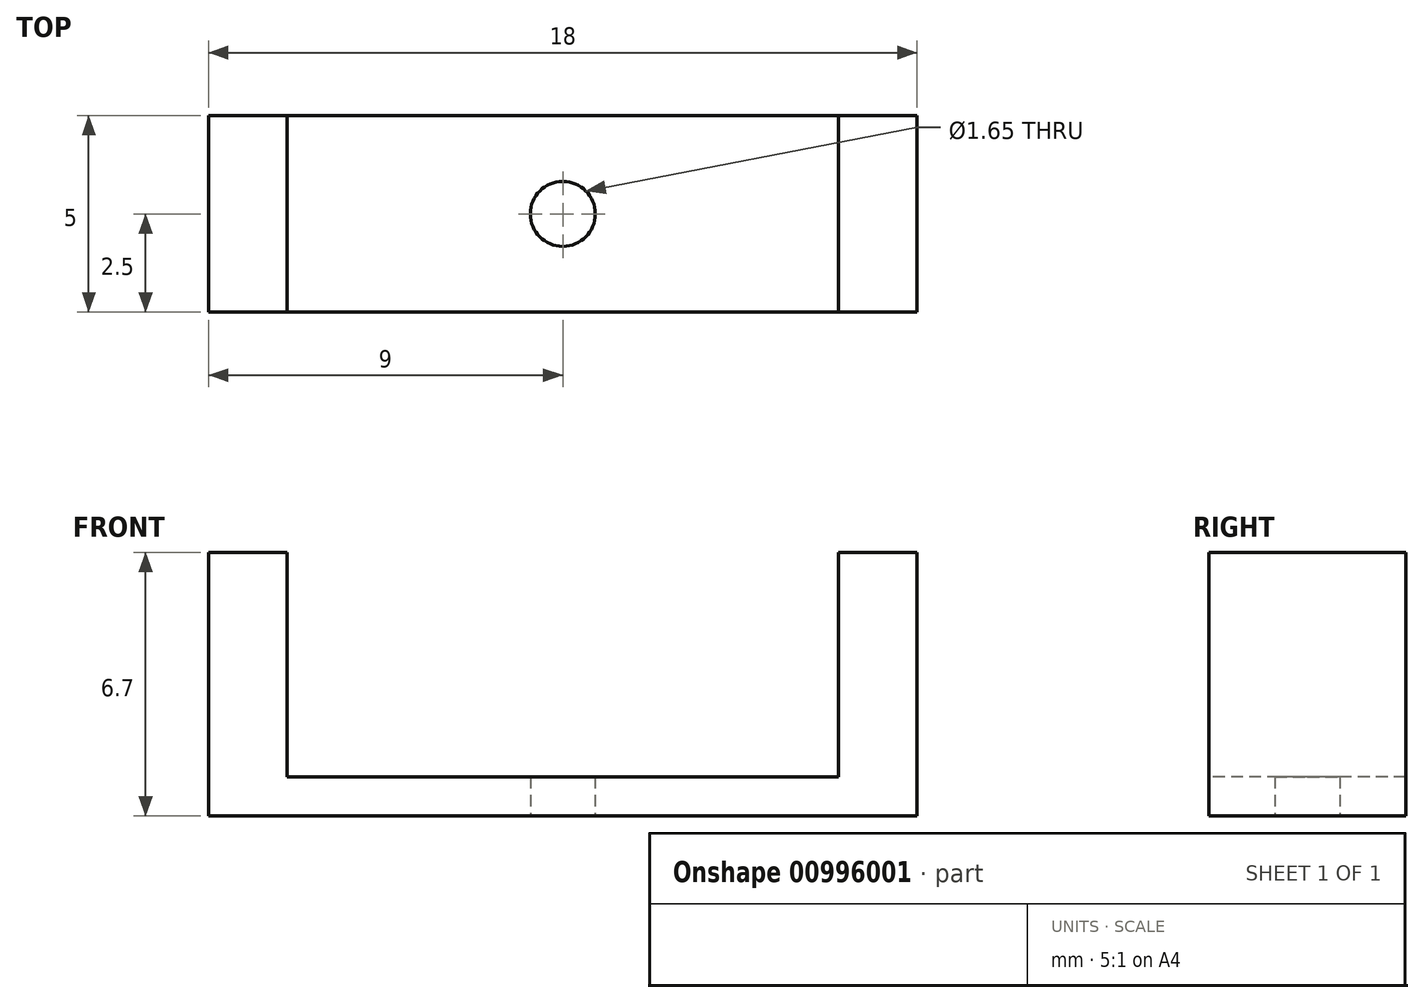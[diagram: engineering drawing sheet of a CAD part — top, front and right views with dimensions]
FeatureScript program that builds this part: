
annotation { "Feature Type Name" : "Feature", "Feature Type Description" : "" }
export const myFeature = defineFeature(function(context is Context, id is Id, definition is map)
    precondition{}
    {
        {
            var Q0;
            Q0=qCreatedBy(makeId("Top.planeOp"),FACE);
            var sketch = newSketch(context, id + "F0", { "sketchPlane" : qUnion([Q0])});
            skLineSegment(sketch, "E0.bottom", {"start": v(9, -2.5) * mm, "end": v(-9, -2.5) * mm});
            skLineSegment(sketch, "E0.top", {"start": v(9, 2.5) * mm, "end": v(-9, 2.5) * mm});
            skLineSegment(sketch, "E0.left", {"start": v(9, -2.5) * mm, "end": v(9, 2.5) * mm});
            skLineSegment(sketch, "E0.right", {"start": v(-9, -2.5) * mm, "end": v(-9, 2.5) * mm});
            skPoint(sketch, "E0.middle", {"position": v(0, 0) * mm});
            skCircle(sketch, "E1", {"center": v(0, 0) * mm, "radius": 0.82 * mm});
            skSolve(sketch);
        }
        {
            var Q0;
            Q0=makeQuery(id+"F0.imprint","IMPRINT",FACE,{"disambiguationData":[TD([[makeQuery(id+"F0.imprint","IMPRINT",EDGE,{"derivedFrom":sQuery(id+"F0.wireOp",EDGE,"E0.bottom")}),-1.0]])]});
            extrude(context, id + "F1", {"entities" : qUnion([Q0]), "depth" : 1 * mm, "offsetDistance" : 25 * mm});
        }
        {
            var Q0;
            Q0=makeQuery(id+"F1.opExtrude","CAP_FACE",FACE,{"disambiguationData":[OSD([sQuery(id+"F0.wireOp",EDGE,"E0.bottom"),sQuery(id+"F0.wireOp",EDGE,"E0.top"),sQuery(id+"F0.wireOp",EDGE,"E0.left"),sQuery(id+"F0.wireOp",EDGE,"E0.right"),sQuery(id+"F0.wireOp",EDGE,"E1")])],"isStart":false});
            var sketch = newSketch(context, id + "F2", { "sketchPlane" : qUnion([Q0])});
            skLineSegment(sketch, "E2.bottom", {"start": v(-9, 2.5) * mm, "end": v(-7, 2.5) * mm});
            skLineSegment(sketch, "E2.top", {"start": v(-9, -2.5) * mm, "end": v(-7, -2.5) * mm});
            skLineSegment(sketch, "E2.left", {"start": v(-9, 2.5) * mm, "end": v(-9, -2.5) * mm});
            skLineSegment(sketch, "E2.right", {"start": v(-7, 2.5) * mm, "end": v(-7, -2.5) * mm});
            skLineSegment(sketch, "E3.bottom", {"start": v(9, 2.5) * mm, "end": v(7, 2.5) * mm});
            skLineSegment(sketch, "E3.top", {"start": v(9, -2.5) * mm, "end": v(7, -2.5) * mm});
            skLineSegment(sketch, "E3.left", {"start": v(9, 2.5) * mm, "end": v(9, -2.5) * mm});
            skLineSegment(sketch, "E3.right", {"start": v(7, 2.5) * mm, "end": v(7, -2.5) * mm});
            skSolve(sketch);
        }
        {
            var Q0;
            Q0=makeQuery(id+"F2.imprint","IMPRINT",FACE,{"disambiguationData":[TD([[makeQuery(id+"F2.imprint","IMPRINT",EDGE,{"derivedFrom":sQuery(id+"F2.wireOp",EDGE,"E2.bottom")}),1.0]])]});
            var Q1;
            Q1=makeQuery(id+"F2.imprint","IMPRINT",FACE,{"disambiguationData":[TD([[makeQuery(id+"F2.imprint","IMPRINT",EDGE,{"derivedFrom":sQuery(id+"F2.wireOp",EDGE,"E3.bottom")}),1.0]])]});
            extrude(context, id + "F3", {"entities" : qUnion([Q0, Q1]), "operationType" : NewBodyOperationType.ADD, "depth" : 5.7 * mm, "offsetDistance" : 25 * mm});
        }
    });
